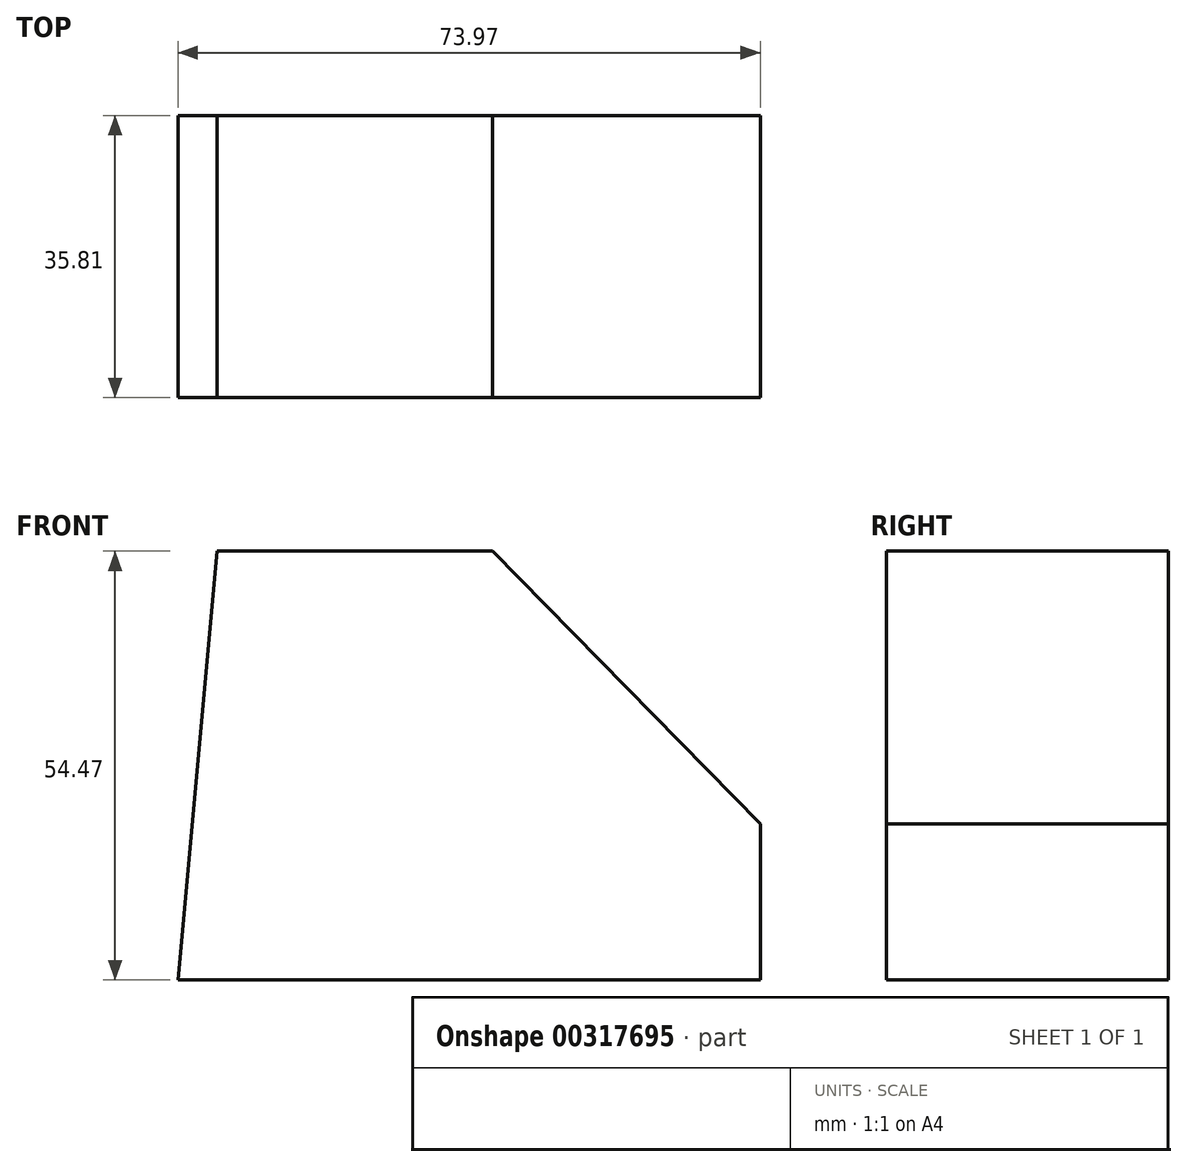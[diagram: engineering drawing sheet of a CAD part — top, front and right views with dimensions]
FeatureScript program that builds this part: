
annotation { "Feature Type Name" : "Feature", "Feature Type Description" : "" }
export const myFeature = defineFeature(function(context is Context, id is Id, definition is map)
    precondition{}
    {
        {
            var Q0;
            Q0=qCreatedBy(makeId("Front.planeOp"),FACE);
            var sketch = newSketch(context, id + "F0", { "sketchPlane" : qUnion([Q0])});
            skLineSegment(sketch, "E0", {"start": v(-45.19, 38.84) * mm, "end": v(-10.21, 38.84) * mm});
            skLineSegment(sketch, "E1", {"start": v(-10.21, 38.84) * mm, "end": v(23.83, 4.18) * mm});
            skLineSegment(sketch, "E2", {"start": v(23.83, 4.18) * mm, "end": v(23.83, -15.63) * mm});
            skLineSegment(sketch, "E3", {"start": v(23.83, -15.63) * mm, "end": v(-50.14, -15.63) * mm});
            skLineSegment(sketch, "E4", {"start": v(-50.14, -15.63) * mm, "end": v(-45.19, 38.84) * mm});
            skSolve(sketch);
        }
        {
            var Q0;
            Q0=makeQuery(id+"F0.imprint","IMPRINT",FACE,{"disambiguationData":[TD([[makeQuery(id+"F0.imprint","IMPRINT",EDGE,{"derivedFrom":sQuery(id+"F0.wireOp",EDGE,"E0")}),-1.0]])]});
            extrude(context, id + "F1", {"entities" : qUnion([Q0]), "depth" : 35.81 * mm});
        }
    });
